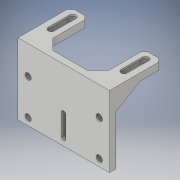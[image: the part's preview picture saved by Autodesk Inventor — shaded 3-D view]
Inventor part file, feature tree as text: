
AUTODESK INVENTOR PART (.ipt)
format: ipt  version: 2019.3 (Build 233278000, 278)  size: 257,536 bytes
history: native  units: mm
features: sketch x7, extrude x5, other x3, rib x2, chamfer x2, reference x1
ambient origin geometry x8: Origin, YZ Plane, XZ Plane, XY Plane, X Axis, Y Axis, Z Axis, Center Point
bodies: Solid1 (feature_tree)
feature tree (20):
  extrude  "Extrusion1"  Depth=9.0mm TaperAngle=0.0deg
  extrude  "Extrusion2"  Depth=10.0mm
  rib  "Rib1"
  rib  "Rib2"
  extrude  "Extrusion3"  Depth=25.0mm
  chamfer  "Chamfer1"  Distance=9.0mm
  chamfer  "Chamfer2"  Distance=4.5mm
  extrude  "Extrusion4"  Depth=7.5mm
  extrude  "Extrusion5"  Depth=7.5mm
  sketch  "Sketch1"  dims[d0=20.0mm d6=9.0mm d7=0.0mm]
  reference  "Reference2"
  sketch  "Sketch2"  dims[d9=65.0mm d10=0.0mm d12=10.0mm]
  sketch  "Sketch3"  dims[d13=25.0mm d14=25.0mm]
  sketch  "Sketch4"  dims[d15=35.0mm]
  sketch  "Sketch5"  dims[d16=20.0mm]
  sketch  "Sketch6"  dims[d17=1.0mm d18=6.0mm d19=0.0mm d20=0.0mm d21=1.0mm d22=1.0mm]
  sketch  "Sketch7"  dims[d23=1.0mm d24=6.0mm d25=0.0mm d26=0.0mm d27=1.0mm d28=1.0mm d30=9.0mm d34=4.5mm d35=7.5mm d36=7.5mm d37=30.0mm d38=10.0mm d39=10.0mm d40=0.0mm d41=3.175mm d42=3.175mm d43=6.35mm d44=3.175mm d45=20.0mm d46=30.0mm d47=15.0mm d48=2.0mm d49=45.0deg d50=5.0mm d51=2.0mm d52=45.0deg d53=9.0mm d54=9.0mm d55=9.0mm d56=9.0mm d57=100.0mm d58=100.0mm d59=50.0mm d60=50.0mm d61=50.0mm d62=50.0mm d63=10.0mm d64=10.0mm d65=14.0mm d66=14.0mm d67=14.0mm d68=14.0mm d69=7.5mm d70=0.0mm d71=13.5mm d73=6.75mm d74=6.75mm d75=6.75mm d76=100.0mm d77=30.0mm d78=30.0mm d79=10.0mm d80=7.5mm d81=0.0mm]
  parser-record x1  (decoder bookkeeping rows leaked as tree rows — omitted from the tree; the rows remain in map.json)
  other  "Assembly.iam"
  other  "Canon_Rebel_T3i:1"
note: 1 file-system path scrubbed to <path> (originals preserved in map.json)
